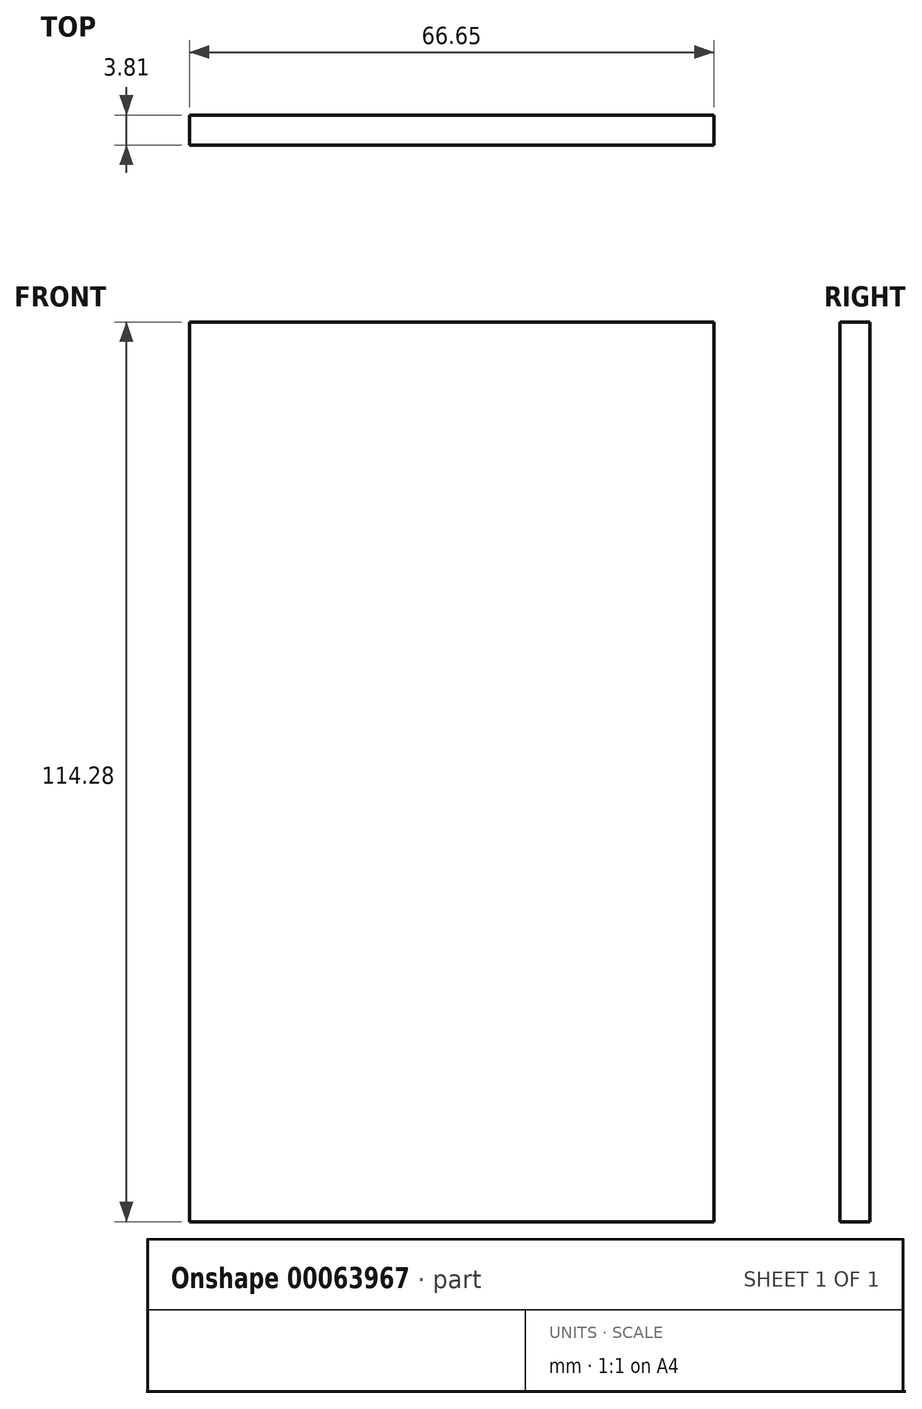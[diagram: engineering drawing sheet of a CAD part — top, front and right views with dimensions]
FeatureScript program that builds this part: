
annotation { "Feature Type Name" : "Feature", "Feature Type Description" : "" }
export const myFeature = defineFeature(function(context is Context, id is Id, definition is map)
    precondition{}
    {
        {
            var Q0;
            Q0=qCreatedBy(makeId("Front.planeOp"),FACE);
            var sketch = newSketch(context, id + "F0", { "sketchPlane" : qUnion([Q0])});
            skLineSegment(sketch, "E0.bottom", {"start": v(-37.6, 62.32) * mm, "end": v(29.04, 62.32) * mm});
            skLineSegment(sketch, "E0.top", {"start": v(-37.6, -51.96) * mm, "end": v(29.04, -51.96) * mm});
            skLineSegment(sketch, "E0.left", {"start": v(-37.6, 62.32) * mm, "end": v(-37.6, -51.96) * mm});
            skLineSegment(sketch, "E0.right", {"start": v(29.04, 62.32) * mm, "end": v(29.04, -51.96) * mm});
            skSolve(sketch);
        }
        {
            var Q0;
            Q0 = qSketchRegion(id + "F0", true);
            extrude(context, id + "F1", {"entities" : qUnion([Q0]), "depth" : 3.8 * mm});
        }
    });
